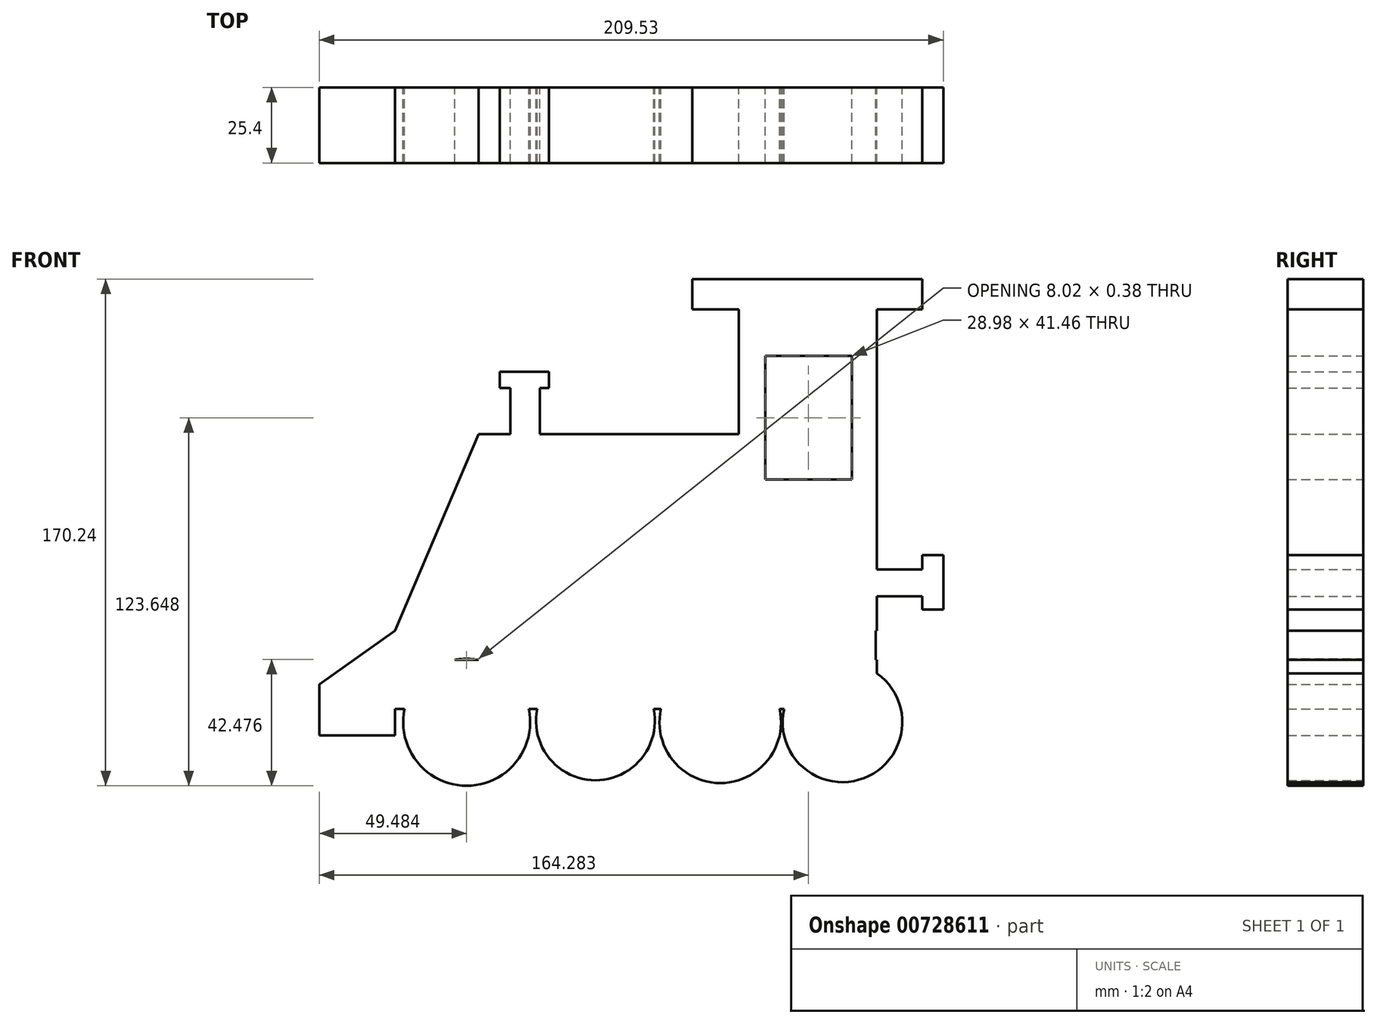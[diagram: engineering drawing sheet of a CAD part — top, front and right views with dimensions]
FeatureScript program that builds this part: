
annotation { "Feature Type Name" : "Feature", "Feature Type Description" : "" }
export const myFeature = defineFeature(function(context is Context, id is Id, definition is map)
    precondition{}
    {
        {
            var Q0;
            Q0=qCreatedBy(makeId("Front.planeOp"),FACE);
            var sketch = newSketch(context, id + "F0", { "sketchPlane" : qUnion([Q0])});
            skLineSegment(sketch, "E0.bottom", {"start": v(-57.73, 34.1) * mm, "end": v(29.65, 34.1) * mm});
            skLineSegment(sketch, "E0.top", {"start": v(-57.73, -31.88) * mm, "end": v(29.65, -31.88) * mm});
            skLineSegment(sketch, "E0.left", {"start": v(-57.73, 34.1) * mm, "end": v(-57.73, -31.88) * mm});
            skLineSegment(sketch, "E0.right", {"start": v(29.65, 34.1) * mm, "end": v(29.65, -31.88) * mm});
            skLineSegment(sketch, "E1.bottom", {"start": v(29.65, -31.88) * mm, "end": v(76.01, -31.88) * mm});
            skLineSegment(sketch, "E1.top", {"start": v(29.65, 76.01) * mm, "end": v(76.01, 76.01) * mm});
            skLineSegment(sketch, "E1.left", {"start": v(29.65, -31.88) * mm, "end": v(29.65, 76.01) * mm});
            skLineSegment(sketch, "E1.right", {"start": v(76.01, -31.88) * mm, "end": v(76.01, 76.01) * mm});
            skLineSegment(sketch, "E2.bottom", {"start": v(38.56, 60.4) * mm, "end": v(67.54, 60.4) * mm});
            skLineSegment(sketch, "E2.top", {"start": v(38.56, 18.95) * mm, "end": v(67.54, 18.95) * mm});
            skLineSegment(sketch, "E2.left", {"start": v(38.56, 60.4) * mm, "end": v(38.56, 18.95) * mm});
            skLineSegment(sketch, "E2.right", {"start": v(67.54, 60.4) * mm, "end": v(67.54, 18.95) * mm});
            skLineSegment(sketch, "E3.bottom", {"start": v(14.04, 76.01) * mm, "end": v(91.17, 76.01) * mm});
            skLineSegment(sketch, "E3.top", {"start": v(14.04, 86.27) * mm, "end": v(91.17, 86.27) * mm});
            skLineSegment(sketch, "E3.left", {"start": v(14.04, 76.01) * mm, "end": v(14.04, 86.27) * mm});
            skLineSegment(sketch, "E3.right", {"start": v(91.17, 76.01) * mm, "end": v(91.17, 86.27) * mm});
            skLineSegment(sketch, "E4.bottom", {"start": v(76.01, -20.28) * mm, "end": v(91.17, -20.28) * mm});
            skLineSegment(sketch, "E4.top", {"start": v(76.01, -11.37) * mm, "end": v(91.17, -11.37) * mm});
            skLineSegment(sketch, "E4.left", {"start": v(76.01, -20.28) * mm, "end": v(76.01, -11.37) * mm});
            skLineSegment(sketch, "E4.right", {"start": v(91.17, -20.28) * mm, "end": v(91.17, -11.37) * mm});
            skLineSegment(sketch, "E5.bottom", {"start": v(91.17, -24.74) * mm, "end": v(98.3, -24.74) * mm});
            skLineSegment(sketch, "E5.top", {"start": v(91.17, -6.46) * mm, "end": v(98.3, -6.46) * mm});
            skLineSegment(sketch, "E5.left", {"start": v(91.17, -24.74) * mm, "end": v(91.17, -6.46) * mm});
            skLineSegment(sketch, "E5.right", {"start": v(98.3, -24.74) * mm, "end": v(98.3, -6.46) * mm});
            skLineSegment(sketch, "E6.bottom", {"start": v(-85.82, -31.88) * mm, "end": v(75.57, -31.88) * mm});
            skLineSegment(sketch, "E6.top", {"start": v(-85.82, -41.68) * mm, "end": v(75.57, -41.68) * mm});
            skLineSegment(sketch, "E6.left", {"start": v(-85.82, -31.88) * mm, "end": v(-85.82, -41.68) * mm});
            skLineSegment(sketch, "E6.right", {"start": v(75.57, -31.88) * mm, "end": v(75.57, -41.68) * mm});
            skLineSegment(sketch, "E7", {"start": v(-85.82, -31.88) * mm, "end": v(-57.73, 34.1) * mm});
            skLineSegment(sketch, "E8.bottom", {"start": v(-47.03, 34.1) * mm, "end": v(-37.23, 34.1) * mm});
            skLineSegment(sketch, "E8.top", {"start": v(-47.03, 49.7) * mm, "end": v(-37.23, 49.7) * mm});
            skLineSegment(sketch, "E8.left", {"start": v(-47.03, 34.1) * mm, "end": v(-47.03, 49.7) * mm});
            skLineSegment(sketch, "E8.right", {"start": v(-37.23, 34.1) * mm, "end": v(-37.23, 49.7) * mm});
            skLineSegment(sketch, "E9.bottom", {"start": v(-34.1, 49.7) * mm, "end": v(-50.6, 49.7) * mm});
            skLineSegment(sketch, "E9.top", {"start": v(-34.1, 55.06) * mm, "end": v(-50.6, 55.06) * mm});
            skLineSegment(sketch, "E9.left", {"start": v(-34.1, 49.7) * mm, "end": v(-34.1, 55.06) * mm});
            skLineSegment(sketch, "E9.right", {"start": v(-50.6, 49.7) * mm, "end": v(-50.6, 55.06) * mm});
            skLineSegment(sketch, "E10.bottom", {"start": v(-85.82, -41.68) * mm, "end": v(76.01, -41.68) * mm});
            skLineSegment(sketch, "E10.top", {"start": v(-85.82, -58.18) * mm, "end": v(76.01, -58.18) * mm});
            skLineSegment(sketch, "E10.left", {"start": v(-85.82, -41.68) * mm, "end": v(-85.82, -58.18) * mm});
            skLineSegment(sketch, "E10.right", {"start": v(76.01, -41.68) * mm, "end": v(76.01, -58.18) * mm});
            skLineSegment(sketch, "E11.bottom", {"start": v(-85.82, -49.93) * mm, "end": v(-111.23, -49.93) * mm});
            skLineSegment(sketch, "E11.top", {"start": v(-85.82, -67.1) * mm, "end": v(-111.23, -67.1) * mm});
            skLineSegment(sketch, "E11.left", {"start": v(-85.82, -49.93) * mm, "end": v(-85.82, -67.1) * mm});
            skLineSegment(sketch, "E11.right", {"start": v(-111.23, -49.93) * mm, "end": v(-111.23, -67.1) * mm});
            skLineSegment(sketch, "E12", {"start": v(-111.23, -49.93) * mm, "end": v(-85.82, -31.88) * mm});
            skCircle(sketch, "E13", {"center": v(-61.75, -62.64) * mm, "radius": 21.33 * mm});
            skCircle(sketch, "E14", {"center": v(-18.5, -62.2) * mm, "radius": 19.96 * mm});
            skCircle(sketch, "E15", {"center": v(23.4, -62.64) * mm, "radius": 20.42 * mm});
            skCircle(sketch, "E16", {"center": v(64.42, -62.64) * mm, "radius": 20.12 * mm});
            skSolve(sketch);
        }
        {
            var Q0;
            Q0 = qSketchRegion(id + "F0", true);
            extrude(context, id + "F1", {"entities" : qUnion([Q0]), "depth" : 25.4 * mm, "offsetDistance" : 25.4 * mm});
        }
    });
